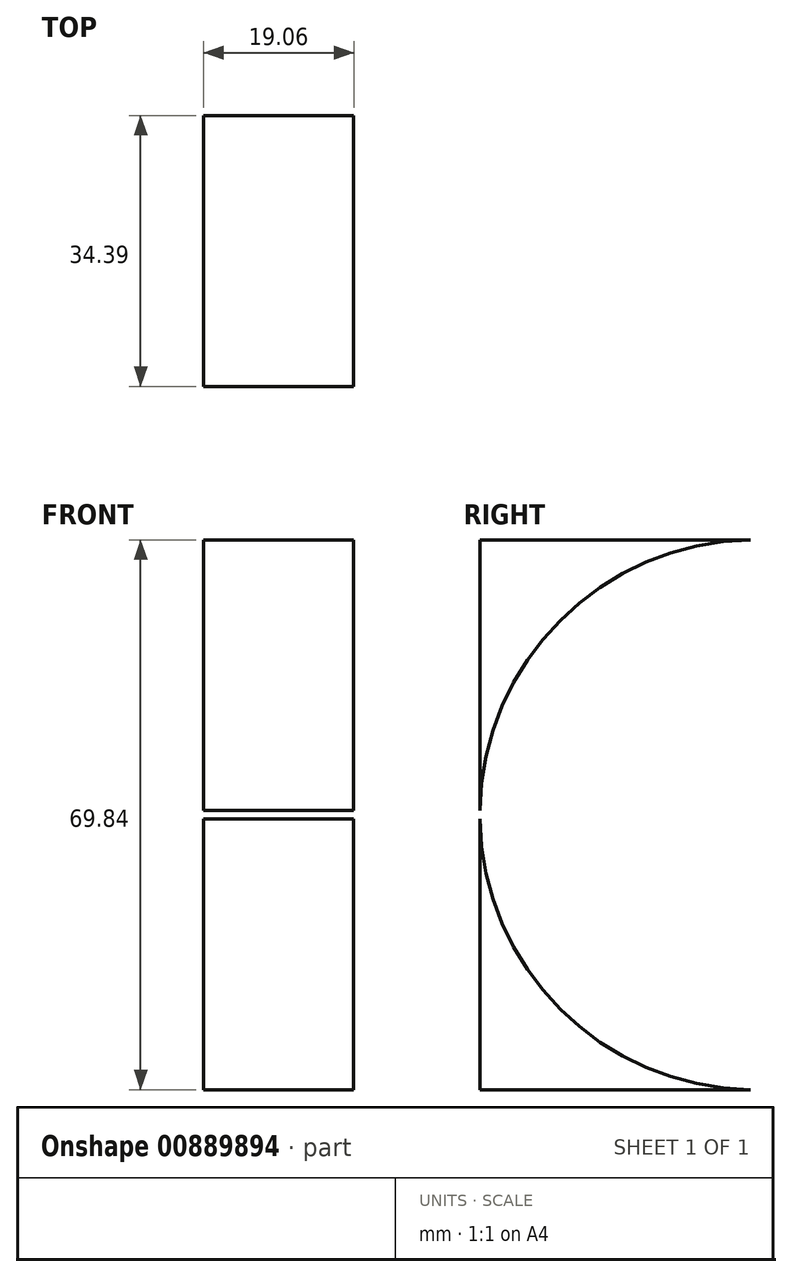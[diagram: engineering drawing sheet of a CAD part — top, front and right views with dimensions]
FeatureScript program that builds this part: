
annotation { "Feature Type Name" : "Feature", "Feature Type Description" : "" }
export const myFeature = defineFeature(function(context is Context, id is Id, definition is map)
    precondition{}
    {
        {
            var Q0;
            Q0=qCreatedBy(makeId("Front.planeOp"),FACE);
            var sketch = newSketch(context, id + "F0", { "sketchPlane" : qUnion([Q0])});
            skLineSegment(sketch, "E0.bottom", {"start": v(9.52, -34.93) * mm, "end": v(-9.53, -34.93) * mm});
            skLineSegment(sketch, "E0.top", {"start": v(9.53, 34.93) * mm, "end": v(-9.52, 34.93) * mm});
            skLineSegment(sketch, "E0.left", {"start": v(9.52, -34.93) * mm, "end": v(9.53, 34.93) * mm});
            skLineSegment(sketch, "E0.right", {"start": v(-9.53, -34.93) * mm, "end": v(-9.52, 34.93) * mm});
            skPoint(sketch, "E0.middle", {"position": v(0, 0) * mm});
            skSolve(sketch);
        }
        {
            var Q0;
            Q0 = qSketchRegion(id + "F0", true);
            extrude(context, id + "F1", {"entities" : qUnion([Q0]), "depth" : 330.2 * mm, "offsetDistance" : 25.4 * mm});
        }
        {
            var Q0;
            Q0=makeQuery(id+"F1.opExtrude","SWEPT_FACE",FACE,{"disambiguationData":[OSD([sQuery(id+"F0.wireOp",EDGE,"E0.left")])]});
            var sketch = newSketch(context, id + "F2", { "sketchPlane" : qUnion([Q0])});
            skLineSegment(sketch, "E1", {"start": v(-330.2, 0) * mm, "end": v(-295.28, 0) * mm, "construction": true});
            skSolve(sketch);
        }
        {
            var Q0;
            Q0=sQuery(id+"F2.wireOp",VERTEX,"E1.end");
            var Q1;
            Q1=makeQuery(id+"F1.opExtrude","SWEPT_BODY",BODY,{"disambiguationData":[OSD([sQuery(id+"F0.wireOp",EDGE,"E0.bottom"),sQuery(id+"F0.wireOp",EDGE,"E0.top"),sQuery(id+"F0.wireOp",EDGE,"E0.left"),sQuery(id+"F0.wireOp",EDGE,"E0.right")])]});
            hole(context, id + "F3", {"style" : HoleStyle.SIMPLE, "endStyle" : HoleEndStyle.THROUGH, "holeDiameter" : 6.35 * mm, "majorDiameter" : 6.35 * mm, "isTappedThrough" : true, "tappedDepth" : 12.7 * mm, "tapClearance" : 3, "locations" : qUnion([Q0]), "scope" : qUnion([Q1])});
        }
        {
            var Q0;
            Q0=makeQuery(id+"F1.opExtrude","SWEPT_FACE",FACE,{"disambiguationData":[OSD([sQuery(id+"F0.wireOp",EDGE,"E0.left")])]});
            var sketch = newSketch(context, id + "F4", { "sketchPlane" : qUnion([Q0])});
            skArc(sketch, "E2", {"start": v(-295.81, -34.93) * mm, "mid": v(-330.2, 0.54) * mm, "end": v(-294.74, 34.93) * mm});
            skSolve(sketch);
        }
        {
            var Q0;
            {var subQ0=sQuery(id+"F4.wireOp",EDGE,"E2");var subQ1=sQuery(id+"F0.wireOp",EDGE,"E0.left");var subQ2=makeQuery(id+"F1.opExtrude","CAP_EDGE",EDGE,{"disambiguationData":[OSD([subQ1])],"isStart":false});var subQ3=makeQuery(id+"F4.imprint","INTERSECT",VERTEX,{"disambiguationData":[OD(1.0)],"derivedFrom":[subQ2,subQ0]});Q0=makeQuery(id+"F4.imprint","IMPRINT",FACE,{"disambiguationData":[TD([[makeQuery(id+"F4.imprint","IMPRINT",EDGE,{"disambiguationData":[TD([[subQ3,-1.0]])],"derivedFrom":subQ0}),1.0]])]});}
            var Q1;
            {var subQ0=sQuery(id+"F4.wireOp",EDGE,"E2");var subQ1=sQuery(id+"F0.wireOp",EDGE,"E0.left");var subQ4=makeQuery(id+"F1.opExtrude","CAP_EDGE",EDGE,{"disambiguationData":[OSD([subQ1])],"isStart":false});var subQ5=makeQuery(id+"F4.imprint","INTERSECT",VERTEX,{"disambiguationData":[OD(0.0)],"derivedFrom":[subQ4,subQ0]});Q1=makeQuery(id+"F4.imprint","IMPRINT",FACE,{"disambiguationData":[TD([[makeQuery(id+"F4.imprint","IMPRINT",EDGE,{"disambiguationData":[TD([[subQ5,1.0]])],"derivedFrom":subQ0}),1.0]])]});}
            extrude(context, id + "F5", {"entities" : qUnion([Q0, Q1]), "operationType" : NewBodyOperationType.REMOVE, "endBound" : BoundingType.THROUGH_ALL, "oppositeDirection" : true, "depth" : 25.4 * mm, "offsetDistance" : 25.4 * mm});
        }
        {
            var Q0;
            Q0=qCreatedBy(makeId("Front.planeOp"),FACE);
            var sketch = newSketch(context, id + "F6", { "sketchPlane" : qUnion([Q0])});
            skLineSegment(sketch, "E3.bottom", {"start": v(60.08, -0.9) * mm, "end": v(85.48, -0.9) * mm});
            skLineSegment(sketch, "E3.top", {"start": v(60.08, -26.3) * mm, "end": v(85.48, -26.3) * mm});
            skLineSegment(sketch, "E3.left", {"start": v(60.08, -0.9) * mm, "end": v(60.08, -26.3) * mm});
            skLineSegment(sketch, "E3.right", {"start": v(85.48, -0.9) * mm, "end": v(85.48, -26.3) * mm});
            skSolve(sketch);
        }
        {
            var Q0;
            Q0=makeQuery(id+"F6.imprint","IMPRINT",FACE,{"disambiguationData":[TD([[makeQuery(id+"F6.imprint","IMPRINT",EDGE,{"derivedFrom":sQuery(id+"F6.wireOp",EDGE,"E3.bottom")}),-1.0]])]});
            extrude(context, id + "F7", {"entities" : qUnion([Q0]), "depth" : 304.8 * mm, "offsetDistance" : 25.4 * mm});
        }
        {
            var Q0;
            Q0=makeQuery(id+"F7.opExtrude","SWEPT_BODY",BODY,{"disambiguationData":[OSD([sQuery(id+"F6.wireOp",EDGE,"E3.bottom"),sQuery(id+"F6.wireOp",EDGE,"E3.top"),sQuery(id+"F6.wireOp",EDGE,"E3.left"),sQuery(id+"F6.wireOp",EDGE,"E3.right")])]});
            deleteBodies(context, id + "F8", {"entities" : qUnion([Q0])});
        }
    });
